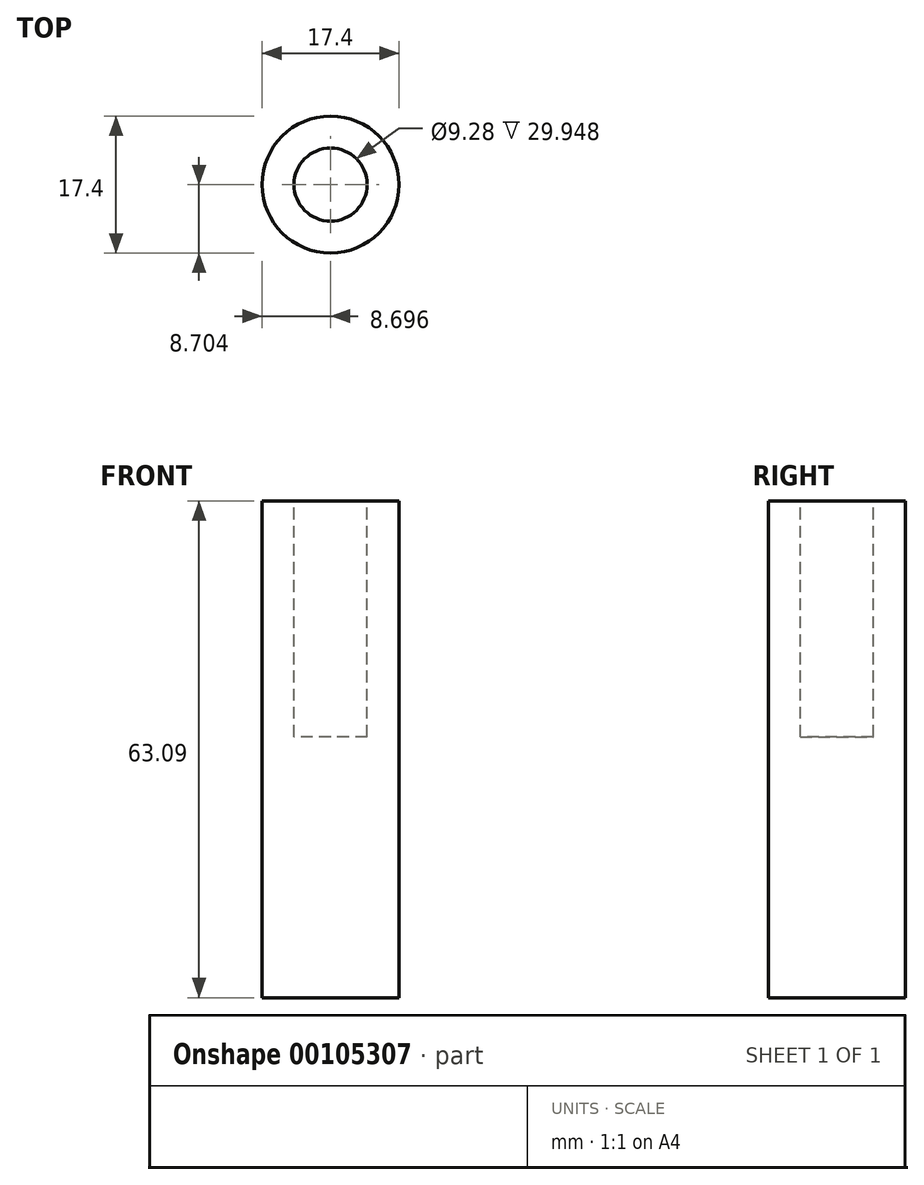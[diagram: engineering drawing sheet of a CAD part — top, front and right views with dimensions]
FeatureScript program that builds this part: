
annotation { "Feature Type Name" : "Feature", "Feature Type Description" : "" }
export const myFeature = defineFeature(function(context is Context, id is Id, definition is map)
    precondition{}
    {
        {
            var Q0;
            Q0=qCreatedBy(makeId("Top.planeOp"),FACE);
            var sketch = newSketch(context, id + "F0", { "sketchPlane" : qUnion([Q0])});
            skCircle(sketch, "E0", {"center": v(-36, 32) * mm, "radius": 8.7 * mm});
            skSolve(sketch);
        }
        {
            var Q0;
            Q0=makeQuery(id+"F0.imprint","IMPRINT",FACE,{"disambiguationData":[TD([[makeQuery(id+"F0.imprint","IMPRINT",EDGE,{"derivedFrom":sQuery(id+"F0.wireOp",EDGE,"E0")}),1.0]])]});
            extrude(context, id + "F1", {"entities" : qUnion([Q0]), "depth" : 63.1 * mm});
        }
        {
            var Q0;
            Q0=makeQuery(id+"F1.opExtrude","CAP_FACE",FACE,{"disambiguationData":[OSD([sQuery(id+"F0.wireOp",EDGE,"E0")])],"isStart":false});
            var sketch = newSketch(context, id + "F2", { "sketchPlane" : qUnion([Q0])});
            skCircle(sketch, "E1", {"center": v(-36, 32) * mm, "radius": 4.64 * mm});
            skSolve(sketch);
        }
        {
            var Q0;
            Q0 = qSketchRegion(id + "F2", true);
            extrude(context, id + "F3", {"entities" : qUnion([Q0]), "operationType" : NewBodyOperationType.REMOVE, "oppositeDirection" : true, "depth" : 29.95 * mm});
        }
    });
